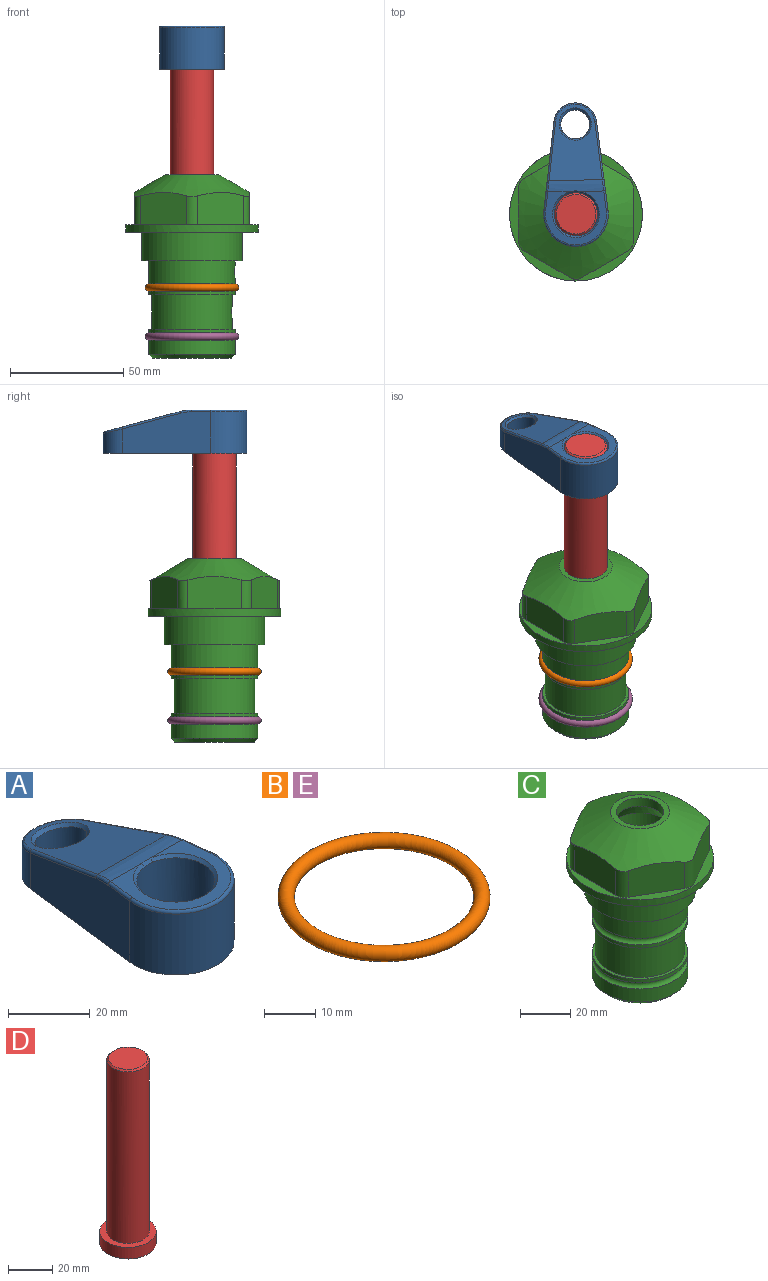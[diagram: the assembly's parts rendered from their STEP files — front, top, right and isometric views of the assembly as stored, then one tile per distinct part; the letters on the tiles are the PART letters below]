
ASSEMBLY  parts=5 mates=4
PART A: 31 faces, bbox 31.7x65.5x19.8 mm
  f0: plane 39.12x18.26mm, normal (0.99,0.12,0), area 612.2mm2, adj f1,f4,f7,f11,f13,f15
  f1: cylinder r=9.53mm len=18.91mm, axis (0,0,-1), area 296.1mm2, adj f0,f2,f7,f17
  f2: plane 39.12x18.26mm, normal (-0.99,0.12,0), area 612.2mm2, adj f1,f4,f7,f12,f14,f16
  f3: cylinder r=6.35mm len=12.7mm, axis (0,0,-1), area 362.4mm2, adj f7,f18
  f4: cylinder r=14.29mm len=28.58mm, axis (0,0,-1), area 882.2mm2, adj f0,f2,f7,f10
  f5: cylinder r=9.53mm len=19.05mm, axis (0,0,-1), area 1092.6mm2, adj f7,f19,f20
  f6: plane 26.99x23.69mm, normal (0,0,1), area 216.2mm2, adj f9,f10,f11,f12,f19
  f7: plane 63.5x28.58mm, normal (0,0,-1), area 661.8mm2, adj f0,f1,f2,f3,f4,f5,f22,f23
  f8: plane 33.52x23.6mm, normal (0,0.26,0.97), area 486mm2, adj f9,f15,f16,f17,f18
  f9: cylinder r=19.05mm len=24.72mm, axis (1,0,0), area 120.4mm2, adj f6,f8,f13,f14,f20
  f10: torus R=13.49mm, axis (0,0,1), area 59mm2, adj f4,f6,f11,f12
  f11: cylinder r=0.79mm len=8.67mm, axis (0.12,-0.99,0), area 10.8mm2, adj f0,f6,f10,f13
  f12: cylinder r=0.79mm len=8.67mm, axis (0.12,0.99,0), area 10.8mm2, adj f2,f6,f10,f14
  f13: bspline ~4.95x1.42mm, area 6.1mm2, adj f0,f9,f11,f15
  f14: bspline ~4.95x1.42mm, area 6.1mm2, adj f2,f9,f12,f16
  f15: cylinder r=0.79mm len=25.95mm, axis (0.12,-0.96,0.26), area 32.9mm2, adj f0,f8,f13,f17
  f16: cylinder r=0.79mm len=25.95mm, axis (0.12,0.96,-0.26), area 32.9mm2, adj f2,f8,f14,f17
  f17: bspline ~18.91x8.38mm, area 30mm2, adj f1,f8,f15,f16
  f18: bspline ~14.29x14.29mm, area 48.3mm2, adj f3,f8
  f19: cone r=9.53mm half-angle=45deg, axis (0,0,1), area 66.5mm2, adj f5,f6,f20
  f20: bspline ~3.22x0.96mm, area 3.5mm2, adj f5,f9,f19
  f21: plane 2.75x2.72mm, normal (0,0,-1), area 2.9mm2, adj f23,f25,f28
  f22: plane 23.05x15.88mm, normal (-0.99,-0.12,0), area 323.6mm2, adj f7,f25,f26,f27,f28,f29
  f23: plane 23.05x15.88mm, normal (0.99,-0.12,0), area 323.6mm2, adj f7,f21,f25,f27,f28,f30
  f24: cylinder r=9.53mm len=10.69mm, axis (0,0,-1), area 114.7mm2, adj f7,f27,f29,f30
  f25: cylinder r=12.7mm len=20.59mm, axis (0,0,-1), area 381.1mm2, adj f7,f21,f22,f23,f26,f28
  f26: plane 2.75x2.72mm, normal (0,0,-1), area 2.9mm2, adj f22,f25,f28
  f27: plane 19.72x18.37mm, normal (0,-0.26,-0.97), area 291.8mm2, adj f22,f23,f24,f28,f29,f30
  f28: cylinder r=15.88mm len=19.92mm, axis (1,0,0), area 54.8mm2, adj f21,f22,f23,f25,f26,f27
  f29: cylinder r=1.59mm len=11mm, axis (0,0,-1), area 34.7mm2, adj f7,f22,f24,f27
  f30: cylinder r=1.59mm len=11mm, axis (0,0,-1), area 34.7mm2, adj f7,f23,f24,f27
PART B: 1 faces, bbox 44.7x44.7x3.2 mm
  f0: torus R=19.05mm, axis (0,0,1), area 1193.9mm2
PART C: 36 faces, bbox 58.7x58.7x81 mm
  f0: cylinder r=17.78mm len=35.56mm, axis (0,0,1), area 1670.8mm2, adj f23,f24,f31
  f1: cylinder r=19.05mm len=38.1mm, axis (0,0,1), area 1191.9mm2, adj f26,f27,f30
  f2: plane 58.66x58.66mm, normal (0,0,-1), area 1150.6mm2, adj f3,f28
  f3: cylinder r=29.33mm len=58.66mm, axis (0,0,-1), area 585.1mm2, adj f2,f4
  f4: plane 58.66x58.66mm, normal (0,0,1), area 475.9mm2, adj f3,f5,f6,f7,f8,f9,f10,f11
  f5: plane 20.32x14.34mm, normal (-0.5,0.87,0), area 324.4mm2, adj f4,f15,f16,f17
  f6: plane 20.32x14.34mm, normal (0.5,0.87,0), area 324.4mm2, adj f4,f14,f15,f17
  f7: plane 23.48x14.34mm, normal (1,0,0), area 324.4mm2, adj f4,f13,f14,f17
  f8: plane 20.32x14.34mm, normal (0.5,-0.87,0), area 324.4mm2, adj f4,f12,f13,f17
  f9: plane 20.32x14.34mm, normal (-0.5,-0.87,0), area 324.4mm2, adj f4,f11,f12,f17
  f10: plane 23.48x14.34mm, normal (-1,0,0), area 324.4mm2, adj f4,f11,f16,f17
  f11: cylinder r=5.08mm len=12.85mm, axis (0,0,-1), area 67.2mm2, adj f4,f9,f10,f17
  f12: cylinder r=5.08mm len=12.85mm, axis (0,0,-1), area 67.2mm2, adj f4,f8,f9,f17
  f13: cylinder r=5.08mm len=12.85mm, axis (0,0,-1), area 67.2mm2, adj f4,f7,f8,f17
  f14: cylinder r=5.08mm len=12.85mm, axis (0,0,-1), area 67.2mm2, adj f4,f6,f7,f17
  f15: cylinder r=5.08mm len=12.85mm, axis (0,0,-1), area 67.2mm2, adj f4,f5,f6,f17
  f16: cylinder r=5.08mm len=12.85mm, axis (0,0,-1), area 67.2mm2, adj f4,f5,f10,f17
  f17: cone r=11.73mm half-angle=60deg, axis (0,0,-1), area 2071.8mm2, adj f5,f6,f7,f8,f9,f10,f11,f12
  f18: plane 23.46x23.46mm, normal (0,0,1), area 147.4mm2, adj f17,f35
  f19: plane 34.93x34.93mm, normal (0,0,-1), area 958mm2, adj f29
  f20: cylinder r=19.05mm len=38.1mm, axis (0,0,1), area 760.1mm2, adj f21,f29
  f21: torus R=19.05mm, axis (0,0,1), area 565.3mm2, adj f20,f22
  f22: cylinder r=19.05mm len=38.1mm, axis (0,0,1), area 190mm2, adj f21,f23
  f23: plane 38.1x38.1mm, normal (0,0,1), area 146.9mm2, adj f0,f22
  f24: plane 38.1x38.1mm, normal (0,0,-1), area 146.9mm2, adj f0,f25
  f25: cylinder r=19.05mm len=38.1mm, axis (0,0,1), area 190mm2, adj f24,f26
  f26: torus R=19.05mm, axis (0,0,1), area 565.3mm2, adj f1,f25
  f27: plane 44.45x44.45mm, normal (0,0,-1), area 411.7mm2, adj f1,f28
  f28: cylinder r=22.23mm len=44.45mm, axis (0,0,1), area 1773.5mm2, adj f2,f27
  f29: cone r=19.05mm half-angle=45deg, axis (0,0,1), area 257.5mm2, adj f19,f20
  f30: cylinder r=3.17mm len=6.75mm, axis (-1,0,0), area 128mm2, adj f1,f33
  f31: cylinder r=3.17mm len=6.35mm, axis (-1,0,0), area 102.5mm2, adj f0,f33
  f32: plane 25.4x25.4mm, normal (0,0,1), area 506.7mm2, adj f33
  f33: cylinder r=12.7mm len=66.42mm, axis (0,0,-1), area 5236.2mm2, adj f30,f31,f32,f34
  f34: cone r=9.53mm half-angle=30deg, axis (0,0,-1), area 443.4mm2, adj f33,f35
  f35: cylinder r=9.53mm len=19.05mm, axis (0,0,-1), area 240.9mm2, adj f18,f34
PART D: 6 faces, bbox 25.4x25.4x101.6 mm
  f0: plane 17.46x17.46mm, normal (0,0,1), area 239.5mm2, adj f5
  f1: plane 25.4x25.4mm, normal (0,0,-1), area 506.7mm2, adj f2
  f2: cylinder r=12.7mm len=25.4mm, axis (0,0,1), area 506.7mm2, adj f1,f3
  f3: plane 25.4x25.4mm, normal (0,0,1), area 221.7mm2, adj f2,f4
  f4: cylinder r=9.53mm len=94.46mm, axis (0,0,1), area 5653mm2, adj f3,f5
  f5: cone r=8.73mm half-angle=45deg, axis (0,0,-1), area 64.4mm2, adj f0,f4
PART E: same geometry as B
PLACE A rot(axis=(0,0,1),0.5deg) t=(0,0,27.55)mm
PLACE B at identity
PLACE C at identity fixed
PLACE D rot(axis=(0,0,1),0.5deg) t=(0,0,27.55)mm
PLACE E t=(0,0,-21.59)mm
MATE fastened E.f0 <-> C.f0  axis (0,0,1) through (0,0,-46.1)mm
MATE fastened D.f2 <-> A.f4  axis (0,0,1) through (0,0,91.05)mm
MATE cylindrical D.f2 <-> C.f0  axis (0,0,-1) through (0,0,-10.55)mm
MATE fastened B.f0 <-> C.f0  axis (0,0,1) through (0,0,-24.51)mm
